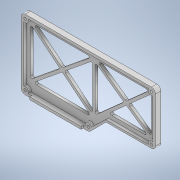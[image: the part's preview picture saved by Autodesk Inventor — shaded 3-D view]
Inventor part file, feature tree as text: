
AUTODESK INVENTOR PART (.ipt)
format: ipt  version: 2021 (Build 250183000, 183)  size: 524,800 bytes
history: native  units: mm
features: sketch x21, extrude x19, fillet x5, hole x2, chamfer x2
ambient origin geometry x8: Origin, YZ Plane, XZ Plane, XY Plane, X Axis, Y Axis, Z Axis, Center Point
bodies: Solid1 (feature_tree)
feature tree (49):
  extrude  "Extrusion1"  Depth=100.0mm
  extrude  "Extrusion2"  Depth=50.0mm
  hole  "Hole1"  [1 undecoded]
  extrude  "Extrusion3"  Depth=50.0mm
  extrude  "Extrusion4"  Depth=3.0mm
  extrude  "Extrusion5"  Depth=3.0mm
  fillet  "Fillet1"  Radius=49.0mm
  extrude  "Extrusion6"  Depth=49.0mm
  extrude  "Extrusion7"  Depth=5.0mm
  extrude  "Extrusion8"  Depth=5.0mm
  chamfer  "Chamfer1"  Distance=3.0mm
  extrude  "Extrusion9"  Depth=12.5mm
  fillet  "Fillet2"  Radius=63.1mm
  extrude  "Extrusion11"  Depth=3.0mm
  extrude  "Extrusion12"  Depth=2.0mm
  chamfer  "Chamfer2"  Distance=3.0mm
  extrude  "Extrusion13"  Depth=3.0mm
  extrude  "Extrusion14"  Depth=1.0mm
  extrude  "Extrusion15"  Depth=1.0mm
  fillet  "Fillet3"  Radius=6.7mm
  fillet  "Fillet4"  Radius=3.0mm
  hole  "Hole2"  [1 undecoded]
  extrude  "Extrusion20"  Depth=2.0mm
  extrude  "Extrusion21"  Depth=12.0mm TaperAngle=0.0deg
  fillet  "Fillet5"  Radius=1.4mm
  extrude  "Extrusion22"  Depth=1.0mm
  extrude  "Extrusion27"  Depth=3.0mm
  extrude  "Extrusion28"  Depth=14.0mm
  sketch  "Sketch1"  dims[d0=52.0mm d1=100.0mm]
  sketch  "Sketch2"  dims[d2=26.0mm d3=50.0mm]
  sketch  "Sketch3"  dims[d4=2.0mm d5=0.0mm d6=3.0mm]
  sketch  "Sketch4"  dims[d7=3.0mm d8=50.0mm]
  sketch  "Sketch5"  dims[d9=3.0mm d10=97.0mm]
  sketch  "Sketch6"  dims[d11=15.0mm d12=3.0mm d13=49.0mm]
  sketch  "Sketch7"  dims[d14=97.0mm d15=49.0mm]
  sketch  "Sketch8"  dims[d16=2.0mm d17=5.0mm]
  sketch  "Sketch9"  dims[d18=2.0mm d19=5.0mm]
  sketch  "Sketch10"  dims[d20=2.0mm]
  sketch  "Sketch12"  dims[d21=5.0mm]
  sketch  "Sketch13"  dims[d22=2.0mm]
  sketch  "Sketch14"  dims[d23=5.0mm]
  sketch  "Sketch15"  dims[d24=2.0mm]
  sketch  "Sketch16"  dims[d25=5.0mm d26=3.0mm d27=0.0mm]
  sketch  "Sketch17"  dims[d28=2.0mm d29=6.0mm d30=5.0mm d31=2.0mm d32=90.0deg d33=10.0mm d34=20.594885mm d35=12.5mm d36=63.1mm]
  sketch  "Sketch23"  dims[d37=3.0mm d38=0.0mm d39=50.673mm]
  sketch  "Sketch24"  dims[d40=3.0mm d41=0.0mm d42=2.0mm]
  sketch  "Sketch25"  dims[d43=2.0mm]
  sketch  "Sketch30"  dims[d44=2.0mm]
  sketch  "Sketch31"  dims[d45=1.5mm d46=3.0mm d47=0.0mm d48=3.0mm d49=7.6mm d50=46.4mm d51=6.7mm d52=3.0mm d53=0.0mm d54=5.0mm d55=2.0mm d56=12.0mm d57=0.0mm d58=1.4mm d59=1.2mm d60=3.0mm d61=14.0mm d62=1.2mm d63=1.4mm d64=12.0mm d65=3.0mm d66=0.0mm d67=1.0mm d68=2.0mm d69=45.0deg d70=1.2mm d71=3.0mm d72=0.0mm d73=1.0mm d77=3.0mm d78=0.0mm d79=3.0mm d80=3.0mm d81=3.0mm d82=3.0mm d83=3.0mm d84=3.0mm d85=3.0mm d86=48.0mm d87=2.0mm d88=0.0mm d89=8.4mm d90=2.0mm d91=45.0deg d92=1.2mm d93=3.0mm d94=0.0mm d95=7.6mm d96=5.0mm d97=0.0mm d98=2.0mm d99=2.0mm d100=2.0mm d101=2.0mm d102=2.0mm d103=2.0mm d104=0.0mm d105=1.0mm d106=1.0mm d107=2.0mm d108=6.0mm d109=5.0mm d110=2.0mm d111=90.0deg d112=4.0mm d113=20.594885mm d146=6.5mm d147=5.0mm d148=2.0mm d149=0.0mm d150=0.3mm d151=0.3mm d152=2.0mm d153=0.0mm d154=3.0mm d155=2.0mm d156=2.0mm d157=2.0mm d158=2.0mm d159=0.0mm d178=1.0mm d179=0.0mm d180=1.0mm d181=0.0mm d74=0.872665mm d75=0.872665mm d76=0.5mm d114=0.75mm d115=20.594885mm d116=0.0625mm d117=0.75mm d118=0.375mm]
note: 2 required parameter values undecoded (feature->parameter linkage not recoverable at this tier; creation-order binding heuristic only, values carry confidence <= 0.55)
